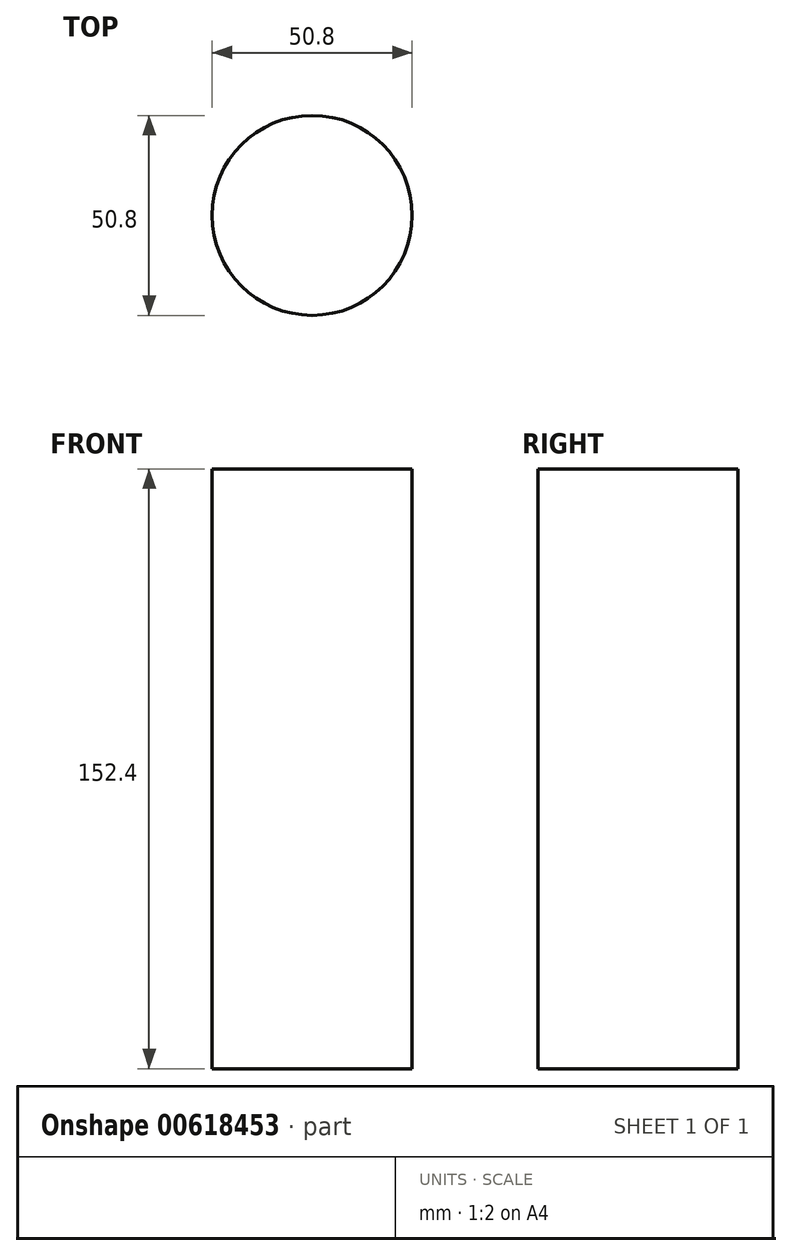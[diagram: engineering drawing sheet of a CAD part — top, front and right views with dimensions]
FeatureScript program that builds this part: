
annotation { "Feature Type Name" : "Feature", "Feature Type Description" : "" }
export const myFeature = defineFeature(function(context is Context, id is Id, definition is map)
    precondition{}
    {
        {
            var Q0;
            Q0=qCreatedBy(makeId("Top.planeOp"),FACE);
            var sketch = newSketch(context, id + "F0", { "sketchPlane" : qUnion([Q0])});
            skCircle(sketch, "E0", {"center": v(0, 0) * mm, "radius": 25.4 * mm});
            skSolve(sketch);
        }
        {
            var Q0;
            Q0 = qSketchRegion(id + "F0", true);
            extrude(context, id + "F1", {"entities" : qUnion([Q0]), "depth" : 152.4 * mm, "offsetDistance" : 25.4 * mm});
        }
        {
            var Q0;
            Q0=makeQuery(id+"F1.opExtrude","CAP_FACE",FACE,{"disambiguationData":[OSD([sQuery(id+"F0.wireOp",EDGE,"E0")])],"isStart":false});
            var sketch = newSketch(context, id + "F2", { "sketchPlane" : qUnion([Q0])});
            skCircle(sketch, "E1", {"center": v(25.4, 0) * mm, "radius": 3.18 * mm});
            skSolve(sketch);
        }
        {
            var Q0;
            {var subQ0=sQuery(id+"F2.wireOp",EDGE,"E1");var subQ1=makeQuery(id+"F1.opExtrude","CAP_EDGE",EDGE,{"disambiguationData":[OSD([sQuery(id+"F0.wireOp",EDGE,"E0")])],"isStart":false});var subQ2=makeQuery(id+"F2.imprint","INTERSECT",VERTEX,{"disambiguationData":[OD(0.0)],"derivedFrom":[subQ1,subQ0]});Q0=makeQuery(id+"F2.imprint","IMPRINT",FACE,{"disambiguationData":[TD([[makeQuery(id+"F2.imprint","IMPRINT",EDGE,{"disambiguationData":[TD([[subQ2,1.0]])],"derivedFrom":subQ0}),-1.0]])]});}
            cPlane(context, id + "F3", {"entities" : qUnion([Q0]), "cplaneType" : CPlaneType.OFFSET, "offset" : 0 * mm, "width" : 152.4 * mm, "height" : 152.4 * mm});
        }
    });
